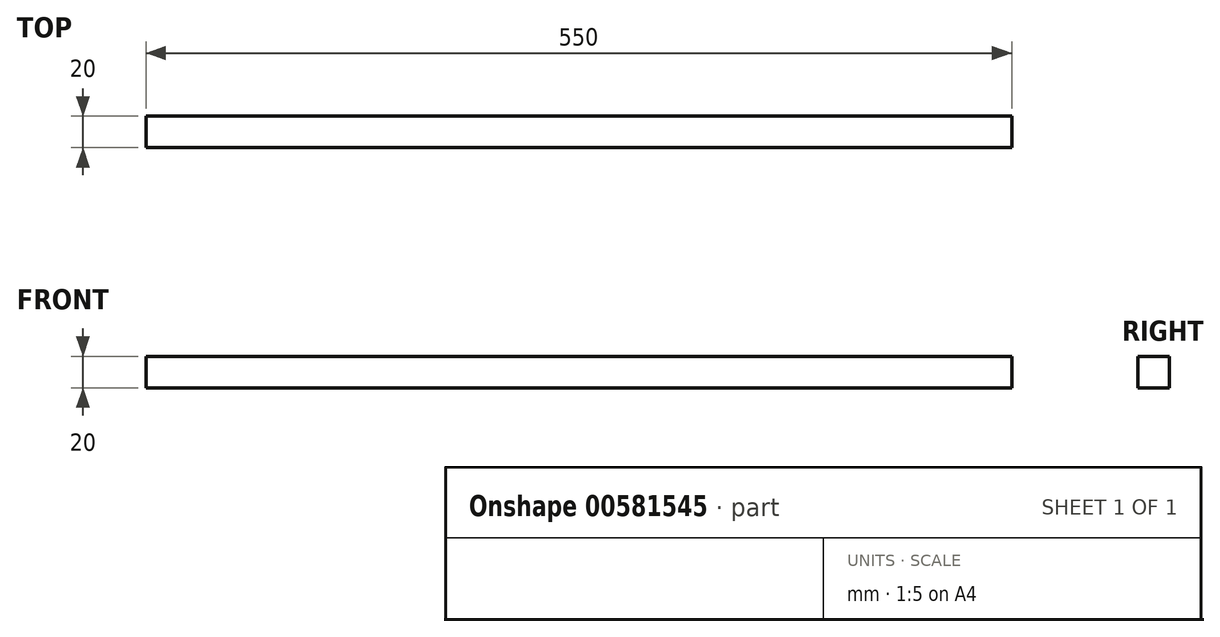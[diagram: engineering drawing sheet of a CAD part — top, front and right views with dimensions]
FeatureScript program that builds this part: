
annotation { "Feature Type Name" : "Feature", "Feature Type Description" : "" }
export const myFeature = defineFeature(function(context is Context, id is Id, definition is map)
    precondition{}
    {
        {
            var Q0;
            Q0=qCreatedBy(makeId("Right.planeOp"),FACE);
            var sketch = newSketch(context, id + "F0", { "sketchPlane" : qUnion([Q0])});
            skLineSegment(sketch, "E0.bottom", {"start": v(-18.8, 20) * mm, "end": v(-38.8, 20) * mm});
            skLineSegment(sketch, "E0.top", {"start": v(-18.8, 0) * mm, "end": v(-38.8, 0) * mm});
            skLineSegment(sketch, "E0.left", {"start": v(-18.8, 20) * mm, "end": v(-18.8, 0) * mm});
            skLineSegment(sketch, "E0.right", {"start": v(-38.8, 20) * mm, "end": v(-38.8, 0) * mm});
            skSolve(sketch);
        }
        {
            var Q0;
            Q0=makeQuery(id+"F0.imprint","IMPRINT",FACE,{"disambiguationData":[TD([[makeQuery(id+"F0.imprint","IMPRINT",EDGE,{"derivedFrom":sQuery(id+"F0.wireOp",EDGE,"E0.bottom")}),1.0]])]});
            extrude(context, id + "F1", {"entities" : qUnion([Q0]), "depth" : 550 * mm, "offsetDistance" : 25 * mm});
        }
    });
